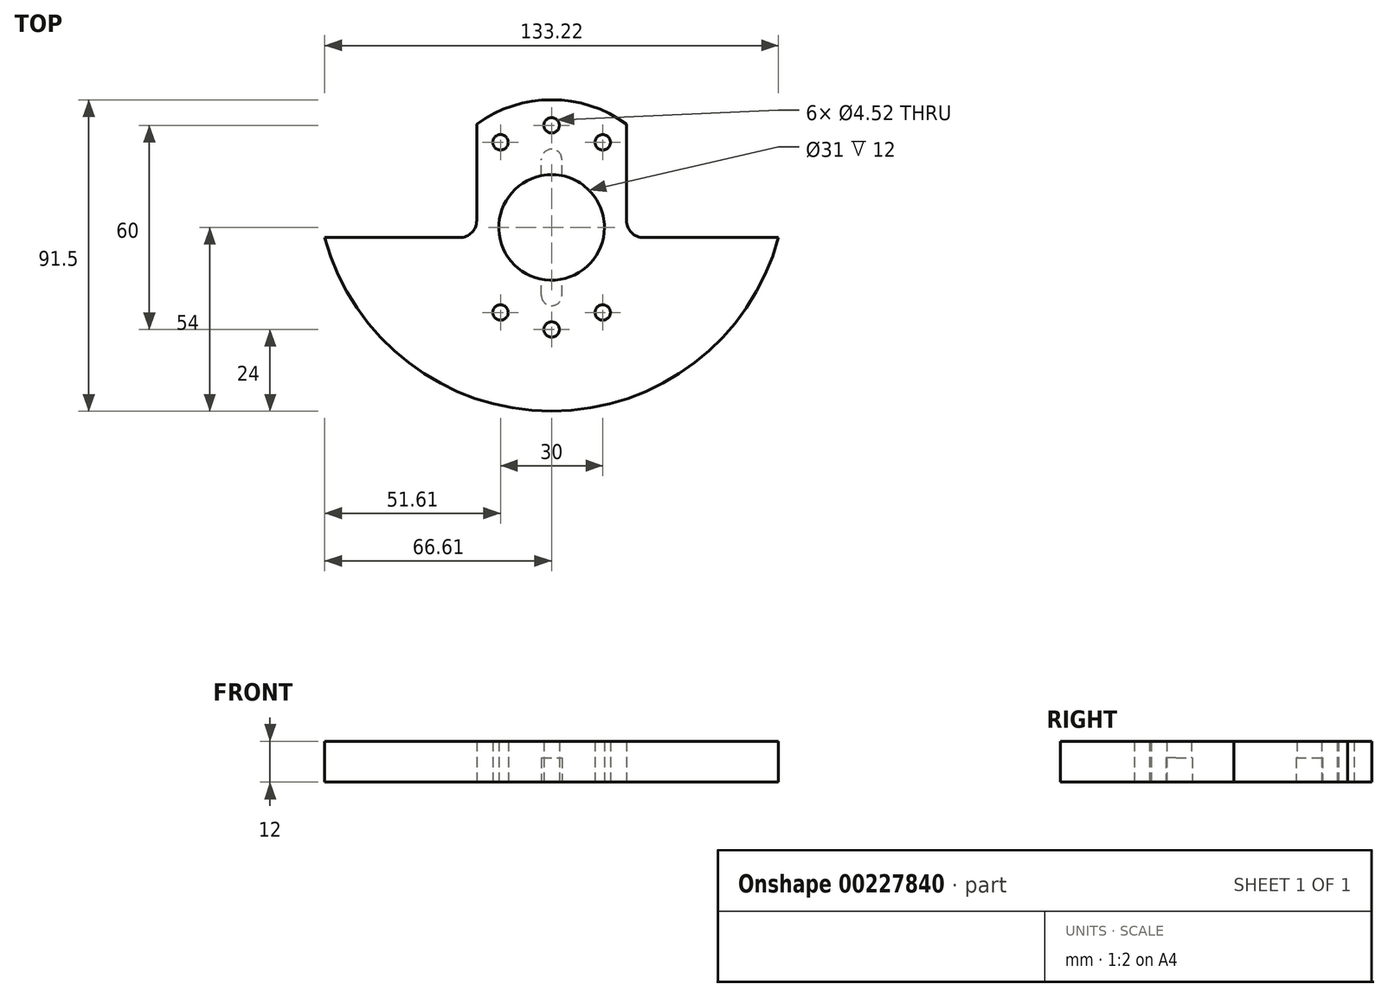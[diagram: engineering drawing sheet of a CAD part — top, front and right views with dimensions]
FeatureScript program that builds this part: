
annotation { "Feature Type Name" : "Feature", "Feature Type Description" : "" }
export const myFeature = defineFeature(function(context is Context, id is Id, definition is map)
    precondition{}
    {
        {
            var Q0;
            Q0=qCreatedBy(makeId("Top.planeOp"),FACE);
            var sketch = newSketch(context, id + "F0", { "sketchPlane" : qUnion([Q0])});
            skArc(sketch, "E0", {"start": v(-15.2, -3) * mm, "mid": v(0, -15.5) * mm, "end": v(15.2, -3) * mm});
            skArc(sketch, "E1", {"start": v(-66.61, -3) * mm, "mid": v(0, -54) * mm, "end": v(66.61, -3) * mm});
            skLineSegment(sketch, "E2", {"start": v(-66.61, -3) * mm, "end": v(-15.2, -3) * mm});
            skLineSegment(sketch, "E3.trimOffspring", {"start": v(15.2, -3) * mm, "end": v(66.61, -3) * mm});
            skCircle(sketch, "E4", {"center": v(-16, -15) * mm, "radius": 2.5 * mm});
            skCircle(sketch, "E5", {"center": v(0, -34) * mm, "radius": 2.5 * mm});
            skCircle(sketch, "E6", {"center": v(0, 15) * mm, "radius": 55 * mm, "construction": true});
            skCircle(sketch, "E7", {"center": v(-16, -31) * mm, "radius": 2.5 * mm});
            skCircle(sketch, "E8.MirrorC", {"center": v(16, -15) * mm, "radius": 2.5 * mm});
            skCircle(sketch, "E9.MirrorC", {"center": v(16, -31) * mm, "radius": 2.5 * mm});
            skCircle(sketch, "E10", {"center": v(0, 15) * mm, "radius": 50 * mm, "construction": true});
            skLineSegment(sketch, "E11.MirrorCS", {"start": v(0, 15) * mm, "end": v(78.85, -30.52) * mm, "construction": true});
            skCircle(sketch, "E12", {"center": v(43.3, -10) * mm, "radius": 20 * mm, "construction": true});
            skSolve(sketch);
        }
        {
            var Q0;
            Q0=qCreatedBy(makeId("Top.planeOp"),FACE);
            cPlane(context, id + "F1", {"entities" : qUnion([Q0]), "cplaneType" : CPlaneType.OFFSET, "offset" : 19 * mm, "width" : 150 * mm, "height" : 150 * mm});
        }
        {
            var Q0;
            Q0=qCreatedBy(id+"F1.planeOp",FACE);
            var sketch = newSketch(context, id + "F2", { "sketchPlane" : qUnion([Q0])});
            skLineSegment(sketch, "E13.0.0", {"start": v(-27, -3) * mm, "end": v(-66.61, -3) * mm});
            skCircle(sketch, "E14.2", {"center": v(-15, -25) * mm, "radius": 2.26 * mm});
            skCircle(sketch, "E14.3", {"center": v(0, -30) * mm, "radius": 2.26 * mm});
            skLineSegment(sketch, "E15", {"start": v(-22, 30.37) * mm, "end": v(-22, 2) * mm});
            skCircle(sketch, "E16", {"center": v(0, 0) * mm, "radius": 15.5 * mm});
            skLineSegment(sketch, "E17.MirrorCS", {"start": v(27, -3) * mm, "end": v(66.61, -3) * mm});
            skArc(sketch, "E18.trimOffspring", {"start": v(22, 30.37) * mm, "mid": v(0, 37.5) * mm, "end": v(-22, 30.37) * mm});
            skCircle(sketch, "E19.MirrorC", {"center": v(15, -25) * mm, "radius": 2.26 * mm});
            skCircle(sketch, "E20.MirrorC", {"center": v(-15, 25) * mm, "radius": 2.26 * mm});
            skCircle(sketch, "E21.MirrorC", {"center": v(15, 25) * mm, "radius": 2.26 * mm});
            skCircle(sketch, "E22.MirrorC", {"center": v(0, 30) * mm, "radius": 2.26 * mm});
            skPoint(sketch, "E23.visualSharp", {"position": v(-22, -3) * mm});
            skArc(sketch, "E23.filletArc", {"start": v(-27, -3) * mm, "mid": v(-23.46, -1.54) * mm, "end": v(-22, 2) * mm});
            skArc(sketch, "E24.MirrorCS", {"start": v(27, -3) * mm, "mid": v(23.46, -1.54) * mm, "end": v(22, 2) * mm});
            skLineSegment(sketch, "E25.MirrorCS", {"start": v(22, 30.37) * mm, "end": v(22, 2) * mm});
            skPoint(sketch, "E26.orphan", {"position": v(22, -3) * mm});
            skArc(sketch, "E27.0", {"start": v(-66.61, -3) * mm, "mid": v(0, -54) * mm, "end": v(66.61, -3) * mm});
            skPoint(sketch, "E28.orphan", {"position": v(-60.24, -3) * mm});
            skPoint(sketch, "E29.orphan", {"position": v(60.24, -3) * mm});
            skSolve(sketch);
        }
        {
            var Q0;
            Q0 = qSketchRegion(id + "F2", true);
            extrude(context, id + "F3", {"entities" : qUnion([Q0]), "depth" : 12 * mm});
        }
        {
            var Q0;
            Q0=qCreatedBy(id+"F1.planeOp",FACE);
            var sketch = newSketch(context, id + "F4", { "sketchPlane" : qUnion([Q0])});
            skArc(sketch, "E30", {"start": v(-3, -20) * mm, "mid": v(0, -23) * mm, "end": v(3, -20) * mm});
            skLineSegment(sketch, "E31", {"start": v(-3, -20) * mm, "end": v(-3, 0) * mm});
            skLineSegment(sketch, "E32.MirrorCS", {"start": v(3, -20) * mm, "end": v(3, 0) * mm});
            skArc(sketch, "E33.MirrorCS", {"start": v(-3, 20) * mm, "mid": v(0, 23) * mm, "end": v(3, 20) * mm});
            skLineSegment(sketch, "E34.MirrorCS", {"start": v(-3, 20) * mm, "end": v(-3, 0) * mm});
            skLineSegment(sketch, "E35.MirrorCS", {"start": v(3, 20) * mm, "end": v(3, 0) * mm});
            skSolve(sketch);
        }
        {
            var Q0;
            Q0 = qSketchRegion(id + "F4", true);
            extrude(context, id + "F5", {"entities" : qUnion([Q0]), "operationType" : NewBodyOperationType.REMOVE, "depth" : 7.1 * mm});
        }
    });
